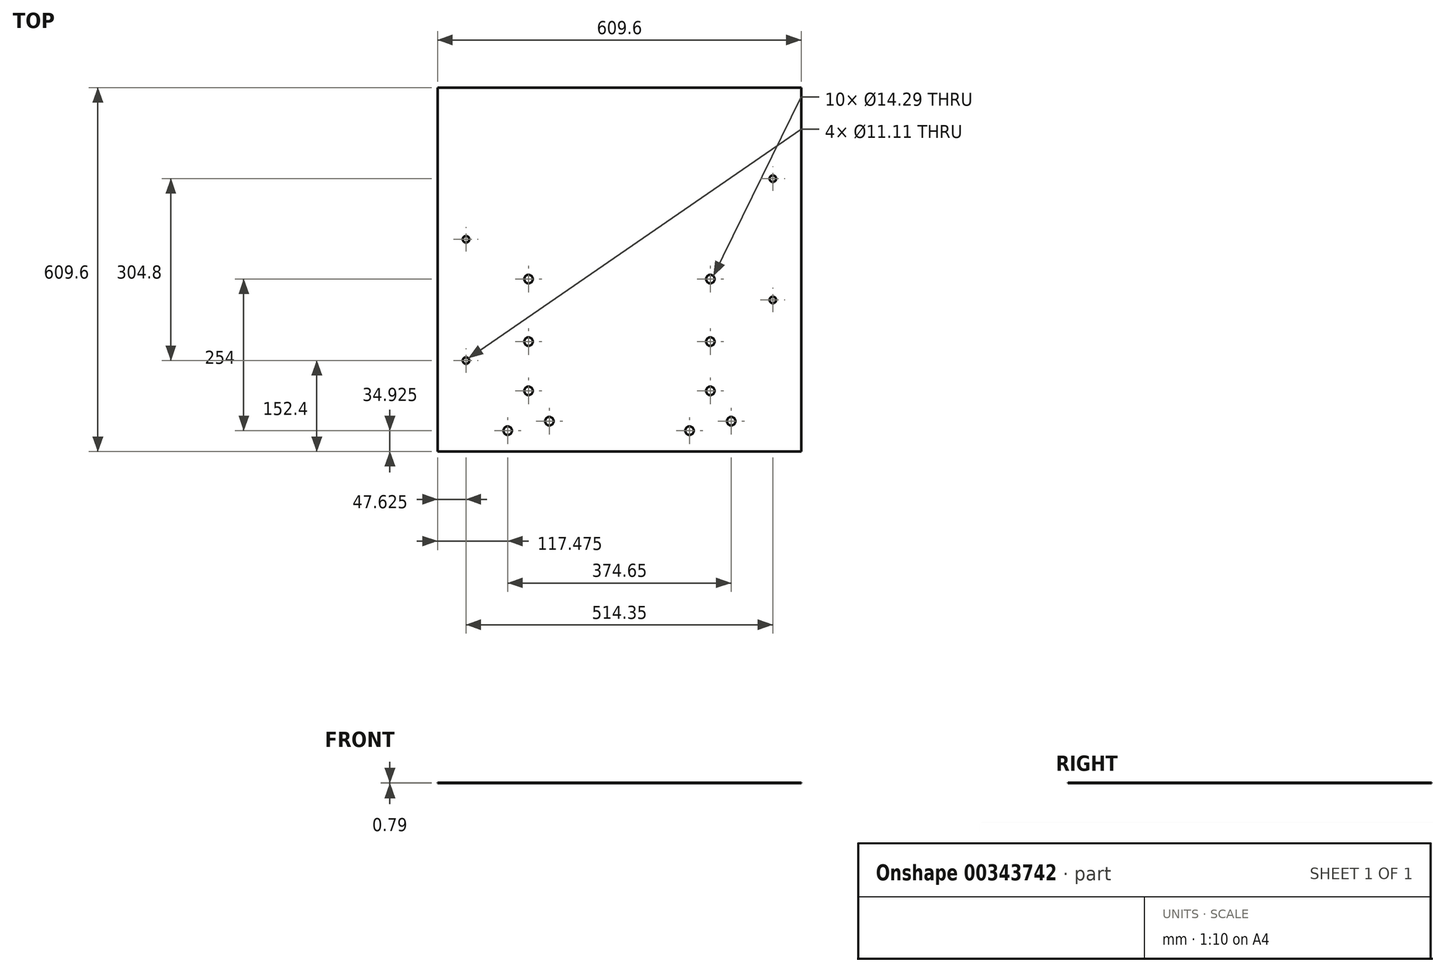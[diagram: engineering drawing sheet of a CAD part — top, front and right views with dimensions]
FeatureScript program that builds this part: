
annotation { "Feature Type Name" : "Feature", "Feature Type Description" : "" }
export const myFeature = defineFeature(function(context is Context, id is Id, definition is map)
    precondition{}
    {
        {
            var Q0;
            Q0=qCreatedBy(makeId("Top.planeOp"),FACE);
            var sketch = newSketch(context, id + "F0", { "sketchPlane" : qUnion([Q0])});
            skLineSegment(sketch, "E0.bottom", {"start": v(0, 0) * mm, "end": v(609.6, 0) * mm});
            skLineSegment(sketch, "E0.top", {"start": v(0, 609.6) * mm, "end": v(609.6, 609.6) * mm});
            skLineSegment(sketch, "E0.left", {"start": v(0, 0) * mm, "end": v(0, 609.6) * mm});
            skLineSegment(sketch, "E0.right", {"start": v(609.6, 0) * mm, "end": v(609.6, 609.6) * mm});
            skSolve(sketch);
        }
        {
            var Q0;
            Q0=makeQuery(id+"F0.imprint","IMPRINT",FACE,{"disambiguationData":[TD([[makeQuery(id+"F0.imprint","IMPRINT",EDGE,{"derivedFrom":sQuery(id+"F0.wireOp",EDGE,"E0.bottom")}),1.0]])]});
            extrude(context, id + "F1", {"entities" : qUnion([Q0]), "depth" : 0.8 * mm});
        }
        {
            var Q0;
            Q0=makeQuery(id+"F1.opExtrude","CAP_FACE",FACE,{"disambiguationData":[OSD([sQuery(id+"F0.wireOp",EDGE,"E0.bottom"),sQuery(id+"F0.wireOp",EDGE,"E0.top"),sQuery(id+"F0.wireOp",EDGE,"E0.left"),sQuery(id+"F0.wireOp",EDGE,"E0.right")])],"isStart":false});
            var sketch = newSketch(context, id + "F2", { "sketchPlane" : qUnion([Q0])});
            skCircle(sketch, "E1", {"center": v(47.63, 152.4) * mm, "radius": 5.56 * mm});
            skCircle(sketch, "E2", {"center": v(47.63, 355.6) * mm, "radius": 5.56 * mm});
            skCircle(sketch, "E3", {"center": v(561.98, 457.2) * mm, "radius": 5.56 * mm});
            skCircle(sketch, "E4", {"center": v(561.98, 254) * mm, "radius": 5.56 * mm});
            skSolve(sketch);
        }
        {
            var Q0;
            Q0=makeQuery(id+"F2.imprint","IMPRINT",FACE,{"disambiguationData":[TD([[makeQuery(id+"F2.imprint","IMPRINT",EDGE,{"derivedFrom":sQuery(id+"F2.wireOp",EDGE,"E1")}),1.0]])]});
            var Q1;
            Q1=makeQuery(id+"F2.imprint","IMPRINT",FACE,{"disambiguationData":[TD([[makeQuery(id+"F2.imprint","IMPRINT",EDGE,{"derivedFrom":sQuery(id+"F2.wireOp",EDGE,"E2")}),1.0]])]});
            var Q2;
            Q2=makeQuery(id+"F2.imprint","IMPRINT",FACE,{"disambiguationData":[TD([[makeQuery(id+"F2.imprint","IMPRINT",EDGE,{"derivedFrom":sQuery(id+"F2.wireOp",EDGE,"E4")}),1.0]])]});
            var Q3;
            Q3=makeQuery(id+"F2.imprint","IMPRINT",FACE,{"disambiguationData":[TD([[makeQuery(id+"F2.imprint","IMPRINT",EDGE,{"derivedFrom":sQuery(id+"F2.wireOp",EDGE,"E3")}),1.0]])]});
            extrude(context, id + "F3", {"entities" : qUnion([Q0, Q1, Q2, Q3]), "operationType" : NewBodyOperationType.REMOVE, "oppositeDirection" : true, "depth" : 25.4 * mm});
        }
        {
            var Q0;
            Q0=makeQuery(id+"F1.opExtrude","CAP_FACE",FACE,{"disambiguationData":[OSD([sQuery(id+"F0.wireOp",EDGE,"E0.bottom"),sQuery(id+"F0.wireOp",EDGE,"E0.top"),sQuery(id+"F0.wireOp",EDGE,"E0.left"),sQuery(id+"F0.wireOp",EDGE,"E0.right")])],"isStart":false});
            var sketch = newSketch(context, id + "F4", { "sketchPlane" : qUnion([Q0])});
            skLineSegment(sketch, "E5", {"start": v(152.4, 0) * mm, "end": v(152.4, 609.6) * mm, "construction": true});
            skCircle(sketch, "E6", {"center": v(117.47, 34.93) * mm, "radius": 7.14 * mm});
            skCircle(sketch, "E7", {"center": v(187.32, 50.8) * mm, "radius": 7.14 * mm});
            skCircle(sketch, "E8", {"center": v(152.4, 101.6) * mm, "radius": 7.14 * mm});
            skCircle(sketch, "E9", {"center": v(152.4, 184.15) * mm, "radius": 7.14 * mm});
            skCircle(sketch, "E10", {"center": v(152.4, 288.93) * mm, "radius": 7.14 * mm});
            skLineSegment(sketch, "E11", {"start": v(304.8, 0) * mm, "end": v(304.8, 609.6) * mm, "construction": true});
            skCircle(sketch, "E12.1.0.0", {"center": v(457.2, 288.93) * mm, "radius": 7.14 * mm});
            skCircle(sketch, "E12.1.0.1", {"center": v(457.2, 184.15) * mm, "radius": 7.14 * mm});
            skCircle(sketch, "E12.1.0.2", {"center": v(457.2, 101.6) * mm, "radius": 7.14 * mm});
            skCircle(sketch, "E12.1.0.3", {"center": v(422.27, 34.93) * mm, "radius": 7.14 * mm});
            skCircle(sketch, "E12.1.0.4", {"center": v(492.12, 50.8) * mm, "radius": 7.14 * mm});
            skLineSegment(sketch, "E12.direction1", {"start": v(152.4, 288.93) * mm, "end": v(457.2, 288.93) * mm, "construction": true});
            skSolve(sketch);
        }
        {
            var Q0;
            Q0=makeQuery(id+"F4.imprint","IMPRINT",FACE,{"disambiguationData":[TD([[makeQuery(id+"F4.imprint","IMPRINT",EDGE,{"derivedFrom":sQuery(id+"F4.wireOp",EDGE,"E7")}),1.0]])]});
            var Q1;
            Q1=makeQuery(id+"F4.imprint","IMPRINT",FACE,{"disambiguationData":[TD([[makeQuery(id+"F4.imprint","IMPRINT",EDGE,{"derivedFrom":sQuery(id+"F4.wireOp",EDGE,"E6")}),1.0]])]});
            var Q2;
            Q2=makeQuery(id+"F4.imprint","IMPRINT",FACE,{"disambiguationData":[TD([[makeQuery(id+"F4.imprint","IMPRINT",EDGE,{"derivedFrom":sQuery(id+"F4.wireOp",EDGE,"E8")}),1.0]])]});
            var Q3;
            Q3=makeQuery(id+"F4.imprint","IMPRINT",FACE,{"disambiguationData":[TD([[makeQuery(id+"F4.imprint","IMPRINT",EDGE,{"derivedFrom":sQuery(id+"F4.wireOp",EDGE,"E9")}),1.0]])]});
            var Q4;
            Q4=makeQuery(id+"F4.imprint","IMPRINT",FACE,{"disambiguationData":[TD([[makeQuery(id+"F4.imprint","IMPRINT",EDGE,{"derivedFrom":sQuery(id+"F4.wireOp",EDGE,"E10")}),1.0]])]});
            var Q5;
            Q5=makeQuery(id+"F4.imprint","IMPRINT",FACE,{"disambiguationData":[TD([[makeQuery(id+"F4.imprint","IMPRINT",EDGE,{"derivedFrom":sQuery(id+"F4.wireOp",EDGE,"99469c5f-eed4-4bda-b829-8e43d59f0d370.MirrorC")}),-1.0]])]});
            var Q6;
            Q6=makeQuery(id+"F4.imprint","IMPRINT",FACE,{"disambiguationData":[TD([[makeQuery(id+"F4.imprint","IMPRINT",EDGE,{"derivedFrom":sQuery(id+"F4.wireOp",EDGE,"cf5fee93-048d-4e7c-bff7-5d6feb919aa70.MirrorC")}),-1.0]])]});
            var Q7;
            Q7=makeQuery(id+"F4.imprint","IMPRINT",FACE,{"disambiguationData":[TD([[makeQuery(id+"F4.imprint","IMPRINT",EDGE,{"derivedFrom":sQuery(id+"F4.wireOp",EDGE,"e178d5ab-6c1a-48aa-8251-bd8876e0b6f30.MirrorC")}),-1.0]])]});
            var Q8;
            Q8=makeQuery(id+"F4.imprint","IMPRINT",FACE,{"disambiguationData":[TD([[makeQuery(id+"F4.imprint","IMPRINT",EDGE,{"derivedFrom":sQuery(id+"F4.wireOp",EDGE,"ab02fdc0-3e5c-4d80-8f89-7c85281f27c90.MirrorC")}),-1.0]])]});
            var Q9;
            Q9=makeQuery(id+"F4.imprint","IMPRINT",FACE,{"disambiguationData":[TD([[makeQuery(id+"F4.imprint","IMPRINT",EDGE,{"derivedFrom":sQuery(id+"F4.wireOp",EDGE,"4ec207aa-f881-40b5-ad5f-906b2cb78b4c0.MirrorC")}),-1.0]])]});
            var Q10;
            Q10=makeQuery(id+"F4.imprint","IMPRINT",FACE,{"disambiguationData":[TD([[makeQuery(id+"F4.imprint","IMPRINT",EDGE,{"derivedFrom":sQuery(id+"F4.wireOp",EDGE,"E12.1.0.3")}),1.0]])]});
            var Q11;
            Q11=makeQuery(id+"F4.imprint","IMPRINT",FACE,{"disambiguationData":[TD([[makeQuery(id+"F4.imprint","IMPRINT",EDGE,{"derivedFrom":sQuery(id+"F4.wireOp",EDGE,"E12.1.0.4")}),1.0]])]});
            var Q12;
            Q12=makeQuery(id+"F4.imprint","IMPRINT",FACE,{"disambiguationData":[TD([[makeQuery(id+"F4.imprint","IMPRINT",EDGE,{"derivedFrom":sQuery(id+"F4.wireOp",EDGE,"E12.1.0.2")}),1.0]])]});
            var Q13;
            Q13=makeQuery(id+"F4.imprint","IMPRINT",FACE,{"disambiguationData":[TD([[makeQuery(id+"F4.imprint","IMPRINT",EDGE,{"derivedFrom":sQuery(id+"F4.wireOp",EDGE,"E12.1.0.1")}),1.0]])]});
            var Q14;
            Q14=makeQuery(id+"F4.imprint","IMPRINT",FACE,{"disambiguationData":[TD([[makeQuery(id+"F4.imprint","IMPRINT",EDGE,{"derivedFrom":sQuery(id+"F4.wireOp",EDGE,"E12.1.0.0")}),1.0]])]});
            extrude(context, id + "F5", {"entities" : qUnion([Q0, Q1, Q2, Q3, Q4, Q5, Q6, Q7, Q8, Q9, Q10, Q11, Q12, Q13, Q14]), "operationType" : NewBodyOperationType.REMOVE, "oppositeDirection" : true, "depth" : 25.4 * mm});
        }
    });
